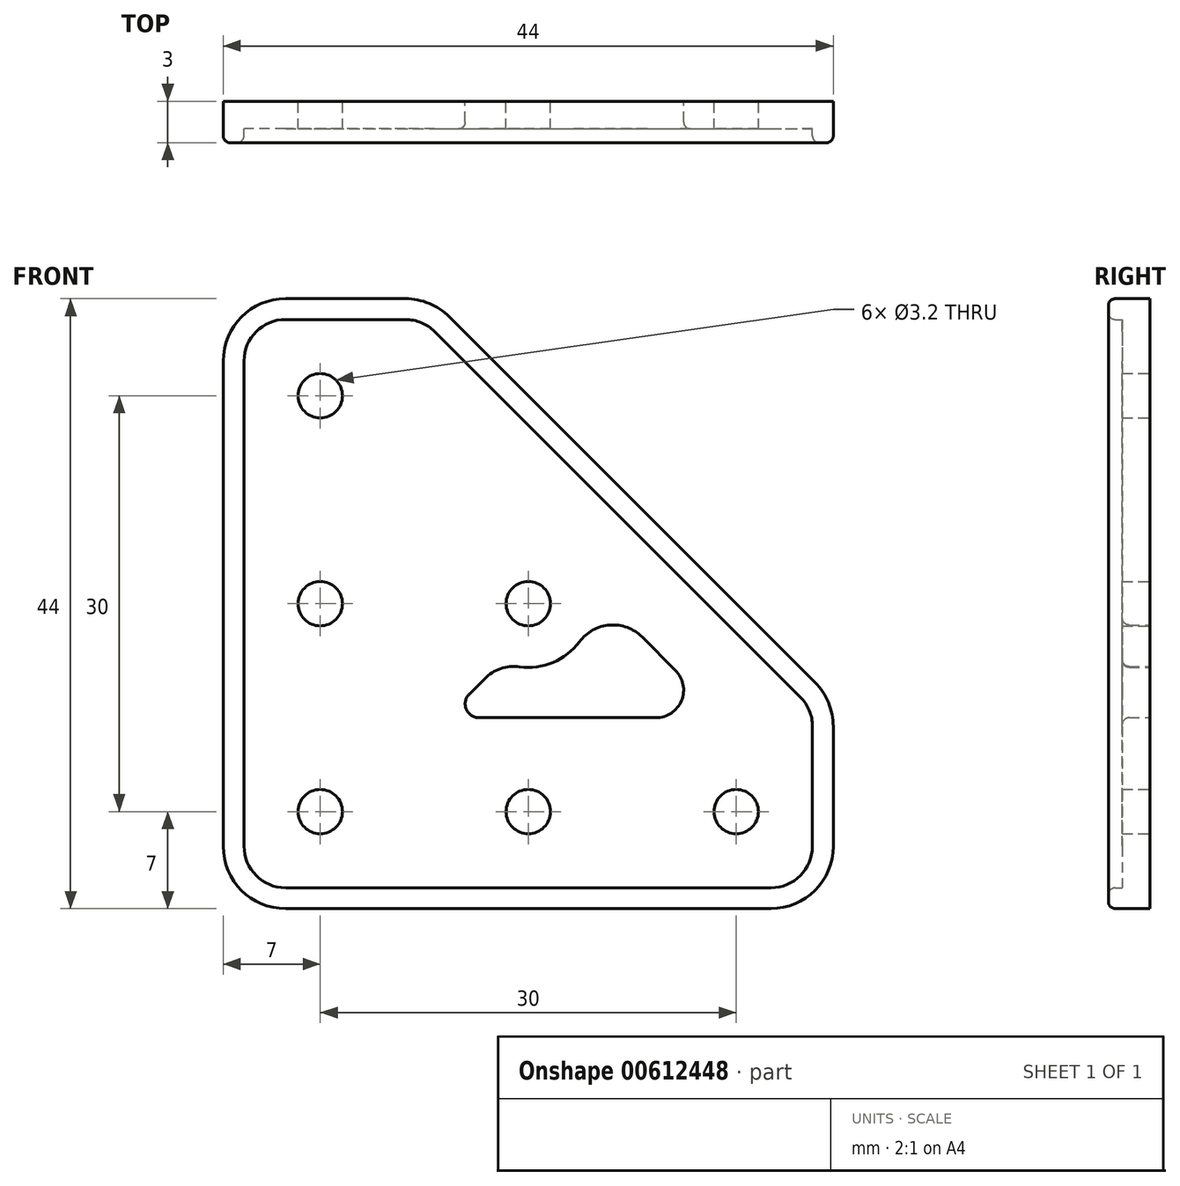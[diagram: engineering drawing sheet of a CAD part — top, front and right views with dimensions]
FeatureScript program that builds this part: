
annotation { "Feature Type Name" : "Feature", "Feature Type Description" : "" }
export const myFeature = defineFeature(function(context is Context, id is Id, definition is map)
    precondition{}
    {
        {
            var Q0;
            Q0=qCreatedBy(makeId("Front.planeOp"),FACE);
            var sketch = newSketch(context, id + "F0", { "sketchPlane" : qUnion([Q0])});
            skLineSegment(sketch, "E0.4", {"start": v(4.5, 0) * mm, "end": v(39.5, 0) * mm});
            skLineSegment(sketch, "E0.8", {"start": v(42.68, 16.32) * mm, "end": v(29.5, 29.5) * mm});
            skCircle(sketch, "E1.0", {"center": v(37, 7) * mm, "radius": 1.6 * mm});
            skCircle(sketch, "E1.1", {"center": v(22, 7) * mm, "radius": 1.6 * mm});
            skCircle(sketch, "E1.2", {"center": v(7, 7) * mm, "radius": 1.6 * mm});
            skCircle(sketch, "E1.3", {"center": v(7, 22) * mm, "radius": 1.6 * mm});
            skCircle(sketch, "E1.4", {"center": v(7, 37) * mm, "radius": 1.6 * mm});
            skCircle(sketch, "E1.5", {"center": v(22, 22) * mm, "radius": 1.6 * mm});
            skLineSegment(sketch, "E2", {"start": v(44, 13.14) * mm, "end": v(44, 4.5) * mm});
            skLineSegment(sketch, "E3", {"start": v(0, 0) * mm, "end": v(29.5, 29.5) * mm, "construction": true});
            skLineSegment(sketch, "E4", {"start": v(44, 15) * mm, "end": v(59, 0) * mm, "construction": true});
            skLineSegment(sketch, "E5", {"start": v(59, 0) * mm, "end": v(44, 0) * mm, "construction": true});
            skPoint(sketch, "E6.visualSharp", {"position": v(44, 0) * mm});
            skArc(sketch, "E6.filletArc", {"start": v(39.5, 0) * mm, "mid": v(42.68, 1.32) * mm, "end": v(44, 4.5) * mm});
            skPoint(sketch, "E7.visualSharp", {"position": v(44, 15) * mm});
            skArc(sketch, "E7.filletArc", {"start": v(44, 13.14) * mm, "mid": v(43.66, 14.86) * mm, "end": v(42.68, 16.32) * mm});
            skLineSegment(sketch, "E8.MirrorCS", {"start": v(16.32, 42.68) * mm, "end": v(29.5, 29.5) * mm});
            skArc(sketch, "E9.MirrorCS", {"start": v(13.14, 44) * mm, "mid": v(14.86, 43.66) * mm, "end": v(16.32, 42.68) * mm});
            skLineSegment(sketch, "E10.MirrorCS", {"start": v(13.14, 44) * mm, "end": v(4.5, 44) * mm});
            skArc(sketch, "E11.MirrorCS", {"start": v(0, 39.5) * mm, "mid": v(1.32, 42.68) * mm, "end": v(4.5, 44) * mm});
            skLineSegment(sketch, "E12.MirrorCS", {"start": v(0, 4.5) * mm, "end": v(0, 39.5) * mm});
            skPoint(sketch, "E13.visualSharp", {"position": v(0, 0) * mm});
            skArc(sketch, "E14.filletArc", {"start": v(0, 4.5) * mm, "mid": v(1.32, 1.32) * mm, "end": v(4.5, 0) * mm});
            skLineSegment(sketch, "E15", {"start": v(44, 15) * mm, "end": v(42.68, 16.32) * mm, "construction": true});
            skLineSegment(sketch, "E16", {"start": v(39.5, 0) * mm, "end": v(44, 0) * mm, "construction": true});
            skSolve(sketch);
        }
        {
            var Q0;
            Q0=makeQuery(id+"F0.imprint","IMPRINT",FACE,{"disambiguationData":[TD([[makeQuery(id+"F0.imprint","IMPRINT",EDGE,{"derivedFrom":sQuery(id+"F0.wireOp",EDGE,"E0.4")}),1.0]])]});
            extrude(context, id + "F1", {"entities" : qUnion([Q0]), "depth" : 2 * mm, "offsetDistance" : 25 * mm});
        }
        {
            var Q0;
            Q0=qCreatedBy(makeId("Front.planeOp"),FACE);
            var sketch = newSketch(context, id + "F2", { "sketchPlane" : qUnion([Q0])});
            skLineSegment(sketch, "E17", {"start": v(32.62, 17.19) * mm, "end": v(30.22, 19.59) * mm});
            skLineSegment(sketch, "E18", {"start": v(31.2, 13.77) * mm, "end": v(18.45, 13.77) * mm});
            skLineSegment(sketch, "E19", {"start": v(26.04, 23.77) * mm, "end": v(18.85, 16.6) * mm, "construction": true});
            skPoint(sketch, "E20.visualSharp", {"position": v(16.04, 13.77) * mm});
            skArc(sketch, "E20.filletArc", {"start": v(17.74, 15.48) * mm, "mid": v(17.53, 14.39) * mm, "end": v(18.45, 13.77) * mm});
            skPoint(sketch, "E21.visualSharp", {"position": v(36.04, 13.77) * mm});
            skArc(sketch, "E21.filletArc", {"start": v(31.2, 13.77) * mm, "mid": v(33.05, 15) * mm, "end": v(32.62, 17.19) * mm});
            skArc(sketch, "E22", {"start": v(18.75, 18.75) * mm, "mid": v(19.96, 17.88) * mm, "end": v(21.38, 17.44) * mm, "construction": true});
            skArc(sketch, "E23", {"start": v(21.38, 17.44) * mm, "mid": v(20.02, 17.31) * mm, "end": v(18.85, 16.6) * mm});
            skArc(sketch, "E24", {"start": v(30.22, 19.59) * mm, "mid": v(27.88, 20.46) * mm, "end": v(25.7, 19.26) * mm});
            skCircle(sketch, "E25", {"center": v(22, 22) * mm, "radius": 1.6 * mm, "construction": true});
            skLineSegment(sketch, "E26", {"start": v(22, 22) * mm, "end": v(23.13, 20.87) * mm, "construction": true});
            skLineSegment(sketch, "E27", {"start": v(23.13, 20.87) * mm, "end": v(25.25, 18.75) * mm, "construction": true});
            skLineSegment(sketch, "E28", {"start": v(30.22, 19.59) * mm, "end": v(26.04, 23.77) * mm, "construction": true});
            skLineSegment(sketch, "E29", {"start": v(18.85, 16.6) * mm, "end": v(17.74, 15.48) * mm});
            skLineSegment(sketch, "E30.0", {"start": v(0, 0) * mm, "end": v(29.5, 29.5) * mm, "construction": true});
            skArc(sketch, "E31", {"start": v(25.7, 19.26) * mm, "mid": v(26.59, 22.34) * mm, "end": v(25.25, 25.25) * mm, "construction": true});
            skArc(sketch, "E32", {"start": v(21.38, 17.44) * mm, "mid": v(23.78, 17.76) * mm, "end": v(25.7, 19.26) * mm});
            skArc(sketch, "E33.MirrorCS", {"start": v(17.44, 21.38) * mm, "mid": v(17.76, 23.78) * mm, "end": v(19.26, 25.7) * mm});
            skArc(sketch, "E34.MirrorCS", {"start": v(19.59, 30.22) * mm, "mid": v(20.46, 27.88) * mm, "end": v(19.26, 25.7) * mm});
            skArc(sketch, "E35.MirrorCS", {"start": v(17.44, 21.38) * mm, "mid": v(17.31, 20.02) * mm, "end": v(16.6, 18.85) * mm});
            skLineSegment(sketch, "E36.MirrorCS", {"start": v(16.6, 18.85) * mm, "end": v(15.48, 17.74) * mm});
            skArc(sketch, "E37.MirrorCS", {"start": v(15.48, 17.74) * mm, "mid": v(14.39, 17.53) * mm, "end": v(13.77, 18.45) * mm});
            skLineSegment(sketch, "E38.MirrorCS", {"start": v(13.77, 31.2) * mm, "end": v(13.77, 18.45) * mm});
            skArc(sketch, "E39.MirrorCS", {"start": v(13.77, 31.2) * mm, "mid": v(15, 33.05) * mm, "end": v(17.19, 32.62) * mm});
            skLineSegment(sketch, "E40.MirrorCS", {"start": v(17.19, 32.62) * mm, "end": v(19.59, 30.22) * mm});
            skSolve(sketch);
        }
        {
            var Q0;
            Q0=makeQuery(id+"F2.imprint","IMPRINT",FACE,{"disambiguationData":[TD([[makeQuery(id+"F2.imprint","IMPRINT",EDGE,{"derivedFrom":sQuery(id+"F2.wireOp",EDGE,"E17")}),1.0]])]});
            var Q1;
            Q1=makeQuery(id+"F2.imprint","IMPRINT",FACE,{"disambiguationData":[TD([[makeQuery(id+"F2.imprint","IMPRINT",EDGE,{"derivedFrom":sQuery(id+"F2.wireOp",EDGE,"E33.MirrorCS")}),1.0]])]});
            extrude(context, id + "F3", {"entities" : qUnion([Q0, Q1]), "operationType" : NewBodyOperationType.REMOVE, "endBound" : BoundingType.THROUGH_ALL, "depth" : 25 * mm, "offsetDistance" : 25 * mm});
        }
        {
            var Q0;
            Q0=makeQuery(id+"F1.opExtrude","CAP_FACE",FACE,{"disambiguationData":[OSD([sQuery(id+"F0.wireOp",EDGE,"E0.4"),sQuery(id+"F0.wireOp",EDGE,"E0.8"),sQuery(id+"F0.wireOp",EDGE,"E1.0"),sQuery(id+"F0.wireOp",EDGE,"E1.1"),sQuery(id+"F0.wireOp",EDGE,"E1.2"),sQuery(id+"F0.wireOp",EDGE,"E1.3"),sQuery(id+"F0.wireOp",EDGE,"E1.4"),sQuery(id+"F0.wireOp",EDGE,"E1.5"),sQuery(id+"F0.wireOp",EDGE,"E2"),sQuery(id+"F0.wireOp",EDGE,"E6.filletArc"),sQuery(id+"F0.wireOp",EDGE,"E7.filletArc"),sQuery(id+"F0.wireOp",EDGE,"E8.MirrorCS"),sQuery(id+"F0.wireOp",EDGE,"E9.MirrorCS"),sQuery(id+"F0.wireOp",EDGE,"E10.MirrorCS"),sQuery(id+"F0.wireOp",EDGE,"E11.MirrorCS"),sQuery(id+"F0.wireOp",EDGE,"E12.MirrorCS"),sQuery(id+"F0.wireOp",EDGE,"E14.filletArc")])],"isStart":false});
            var sketch = newSketch(context, id + "F4", { "sketchPlane" : qUnion([Q0])});
            skLineSegment(sketch, "E41.0", {"start": v(0, 4.5) * mm, "end": v(0, 39.5) * mm});
            skArc(sketch, "E41.1", {"start": v(0, 39.5) * mm, "mid": v(1.32, 42.68) * mm, "end": v(4.5, 44) * mm});
            skLineSegment(sketch, "E41.2", {"start": v(13.14, 44) * mm, "end": v(4.5, 44) * mm});
            skArc(sketch, "E41.3", {"start": v(13.14, 44) * mm, "mid": v(14.86, 43.66) * mm, "end": v(16.32, 42.68) * mm});
            skLineSegment(sketch, "E41.4", {"start": v(16.32, 42.68) * mm, "end": v(29.5, 29.5) * mm});
            skLineSegment(sketch, "E41.5", {"start": v(42.68, 16.32) * mm, "end": v(29.5, 29.5) * mm});
            skArc(sketch, "E41.6", {"start": v(44, 13.14) * mm, "mid": v(43.66, 14.86) * mm, "end": v(42.68, 16.32) * mm});
            skLineSegment(sketch, "E41.7", {"start": v(44, 13.14) * mm, "end": v(44, 4.5) * mm});
            skArc(sketch, "E41.8", {"start": v(39.5, 0) * mm, "mid": v(42.68, 1.32) * mm, "end": v(44, 4.5) * mm});
            skLineSegment(sketch, "E41.9", {"start": v(4.5, 0) * mm, "end": v(39.5, 0) * mm});
            skArc(sketch, "E41.10", {"start": v(0, 4.5) * mm, "mid": v(1.32, 1.32) * mm, "end": v(4.5, 0) * mm});
            skArc(sketch, "E42.0", {"start": v(42.5, 13.14) * mm, "mid": v(42.27, 14.28) * mm, "end": v(41.62, 15.26) * mm});
            skLineSegment(sketch, "E42.1", {"start": v(42.5, 13.14) * mm, "end": v(42.5, 4.5) * mm});
            skArc(sketch, "E42.2", {"start": v(39.5, 1.5) * mm, "mid": v(41.62, 2.38) * mm, "end": v(42.5, 4.5) * mm});
            skLineSegment(sketch, "E42.3", {"start": v(4.5, 1.5) * mm, "end": v(39.5, 1.5) * mm});
            skArc(sketch, "E42.4", {"start": v(1.5, 4.5) * mm, "mid": v(2.38, 2.38) * mm, "end": v(4.5, 1.5) * mm});
            skLineSegment(sketch, "E42.5", {"start": v(41.62, 15.26) * mm, "end": v(28.44, 28.44) * mm});
            skLineSegment(sketch, "E42.6", {"start": v(15.26, 41.62) * mm, "end": v(28.44, 28.44) * mm});
            skArc(sketch, "E42.7", {"start": v(13.14, 42.5) * mm, "mid": v(14.28, 42.27) * mm, "end": v(15.26, 41.62) * mm});
            skLineSegment(sketch, "E42.8", {"start": v(13.14, 42.5) * mm, "end": v(4.5, 42.5) * mm});
            skArc(sketch, "E42.9", {"start": v(1.5, 39.5) * mm, "mid": v(2.38, 41.62) * mm, "end": v(4.5, 42.5) * mm});
            skLineSegment(sketch, "E42.10", {"start": v(1.5, 4.5) * mm, "end": v(1.5, 39.5) * mm});
            skSolve(sketch);
        }
        {
            var Q0;
            Q0=makeQuery(id+"F4.imprint","IMPRINT",FACE,{"disambiguationData":[TD([[makeQuery(id+"F4.imprint","IMPRINT",EDGE,{"derivedFrom":sQuery(id+"F4.wireOp",EDGE,"E41.0")}),-1.0]])]});
            extrude(context, id + "F5", {"entities" : qUnion([Q0]), "operationType" : NewBodyOperationType.ADD, "depth" : 1 * mm, "offsetDistance" : 25 * mm});
        }
        {
            var Q0;
            Q0=makeQuery(id+"F5.opExtrude","CAP_EDGE",EDGE,{"disambiguationData":[OSD([sQuery(id+"F4.wireOp",EDGE,"E42.10")])],"isStart":false});
            var Q1;
            Q1=makeQuery(id+"F5.opExtrude","CAP_EDGE",EDGE,{"disambiguationData":[OSD([sQuery(id+"F4.wireOp",EDGE,"E41.0")])],"isStart":false});
            var Q2;
            Q2=makeQuery(id+"F3.boolean.opBoolean","INTERSECT",EDGE,{"derivedFrom":[makeQuery(id+"F1.opExtrude","CAP_FACE",FACE,{"disambiguationData":[OSD([sQuery(id+"F0.wireOp",EDGE,"E0.4"),sQuery(id+"F0.wireOp",EDGE,"E0.8"),sQuery(id+"F0.wireOp",EDGE,"E1.0"),sQuery(id+"F0.wireOp",EDGE,"E1.1"),sQuery(id+"F0.wireOp",EDGE,"E1.2"),sQuery(id+"F0.wireOp",EDGE,"E1.3"),sQuery(id+"F0.wireOp",EDGE,"E1.4"),sQuery(id+"F0.wireOp",EDGE,"E1.5"),sQuery(id+"F0.wireOp",EDGE,"E2"),sQuery(id+"F0.wireOp",EDGE,"E6.filletArc"),sQuery(id+"F0.wireOp",EDGE,"E7.filletArc"),sQuery(id+"F0.wireOp",EDGE,"E8.MirrorCS"),sQuery(id+"F0.wireOp",EDGE,"E9.MirrorCS"),sQuery(id+"F0.wireOp",EDGE,"E10.MirrorCS"),sQuery(id+"F0.wireOp",EDGE,"E11.MirrorCS"),sQuery(id+"F0.wireOp",EDGE,"E12.MirrorCS"),sQuery(id+"F0.wireOp",EDGE,"E14.filletArc")])],"isStart":false}),makeQuery(id+"F3.opExtrude","SWEPT_FACE",FACE,{"disambiguationData":[OSD([sQuery(id+"F2.wireOp",EDGE,"E23")])]})]});
            var Q3;
            Q3=makeQuery(id+"F3.boolean.opBoolean","INTERSECT",EDGE,{"derivedFrom":[makeQuery(id+"F1.opExtrude","CAP_FACE",FACE,{"disambiguationData":[OSD([sQuery(id+"F0.wireOp",EDGE,"E0.4"),sQuery(id+"F0.wireOp",EDGE,"E0.8"),sQuery(id+"F0.wireOp",EDGE,"E1.0"),sQuery(id+"F0.wireOp",EDGE,"E1.1"),sQuery(id+"F0.wireOp",EDGE,"E1.2"),sQuery(id+"F0.wireOp",EDGE,"E1.3"),sQuery(id+"F0.wireOp",EDGE,"E1.4"),sQuery(id+"F0.wireOp",EDGE,"E1.5"),sQuery(id+"F0.wireOp",EDGE,"E2"),sQuery(id+"F0.wireOp",EDGE,"E6.filletArc"),sQuery(id+"F0.wireOp",EDGE,"E7.filletArc"),sQuery(id+"F0.wireOp",EDGE,"E8.MirrorCS"),sQuery(id+"F0.wireOp",EDGE,"E9.MirrorCS"),sQuery(id+"F0.wireOp",EDGE,"E10.MirrorCS"),sQuery(id+"F0.wireOp",EDGE,"E11.MirrorCS"),sQuery(id+"F0.wireOp",EDGE,"E12.MirrorCS"),sQuery(id+"F0.wireOp",EDGE,"E14.filletArc")])],"isStart":false}),makeQuery(id+"F3.opExtrude","SWEPT_FACE",FACE,{"disambiguationData":[OSD([sQuery(id+"F2.wireOp",EDGE,"E35.MirrorCS")])]})]});
            fillet(context, id + "F6", {"entities" : qUnion([Q0, Q1, Q2, Q3]), "radius" : 0.5 * mm, "tangentPropagation" : true, "allowEdgeOverflow" : false});
        }
    });
